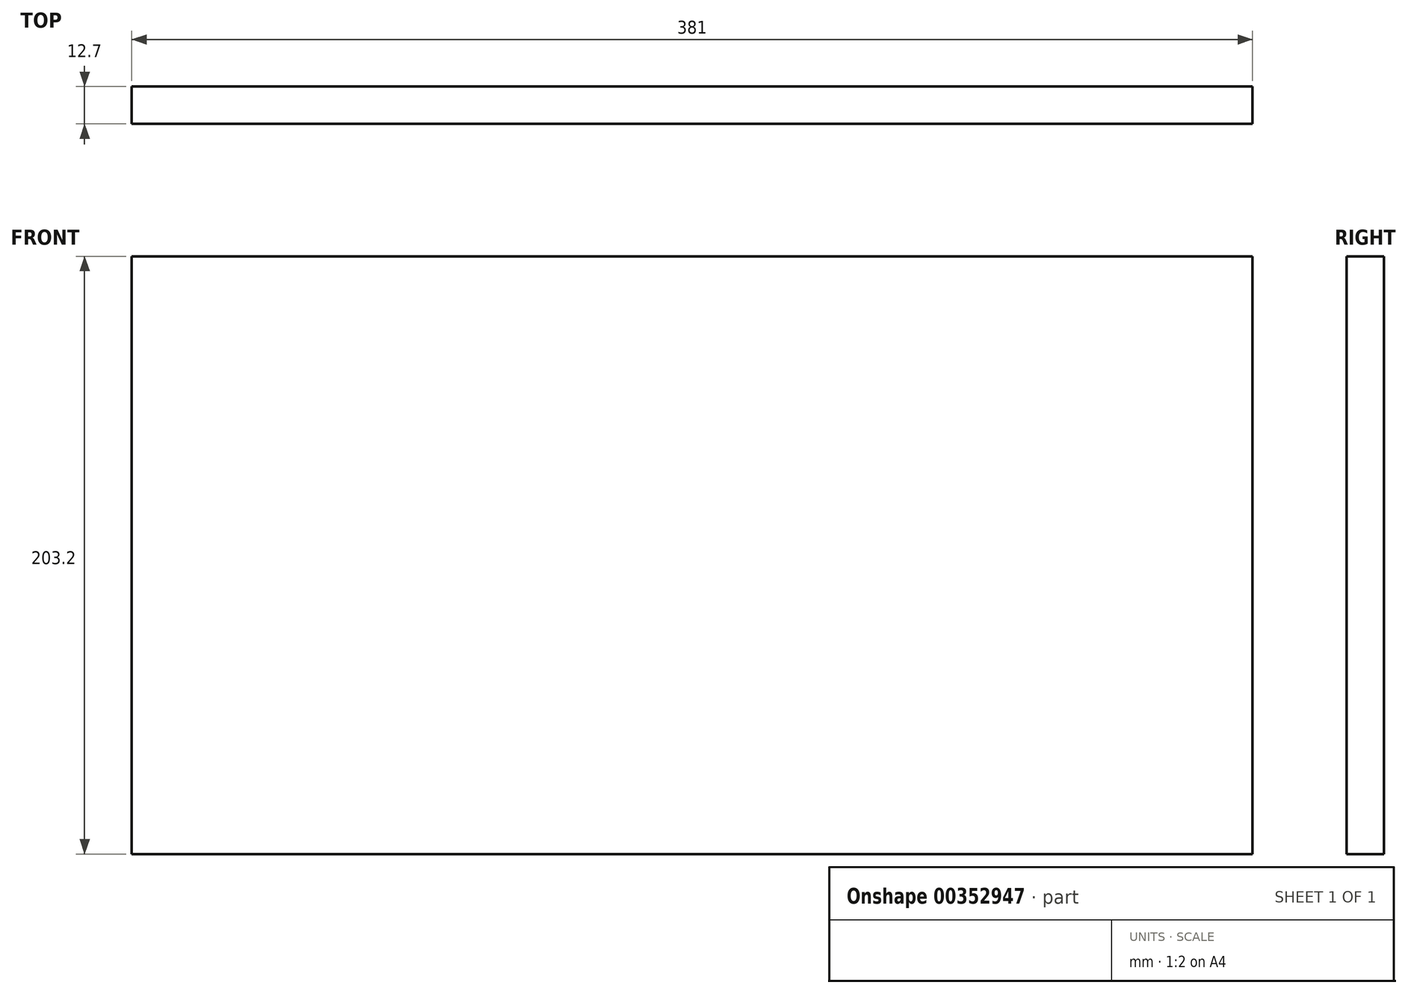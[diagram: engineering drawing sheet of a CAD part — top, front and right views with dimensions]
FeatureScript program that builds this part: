
annotation { "Feature Type Name" : "Feature", "Feature Type Description" : "" }
export const myFeature = defineFeature(function(context is Context, id is Id, definition is map)
    precondition{}
    {
        {
            var Q0;
            Q0=qCreatedBy(makeId("Front.planeOp"),FACE);
            var sketch = newSketch(context, id + "F0", { "sketchPlane" : qUnion([Q0])});
            skLineSegment(sketch, "E0.bottom", {"start": v(190.5, -101.6) * mm, "end": v(-190.5, -101.6) * mm});
            skLineSegment(sketch, "E0.top", {"start": v(190.5, 101.6) * mm, "end": v(-190.5, 101.6) * mm});
            skLineSegment(sketch, "E0.left", {"start": v(190.5, -101.6) * mm, "end": v(190.5, 101.6) * mm});
            skLineSegment(sketch, "E0.right", {"start": v(-190.5, -101.6) * mm, "end": v(-190.5, 101.6) * mm});
            skPoint(sketch, "E0.middle", {"position": v(0, 0) * mm});
            skSolve(sketch);
        }
        {
            var Q0;
            Q0 = qSketchRegion(id + "F0", true);
            extrude(context, id + "F1", {"entities" : qUnion([Q0]), "depth" : 12.7 * mm});
        }
    });
